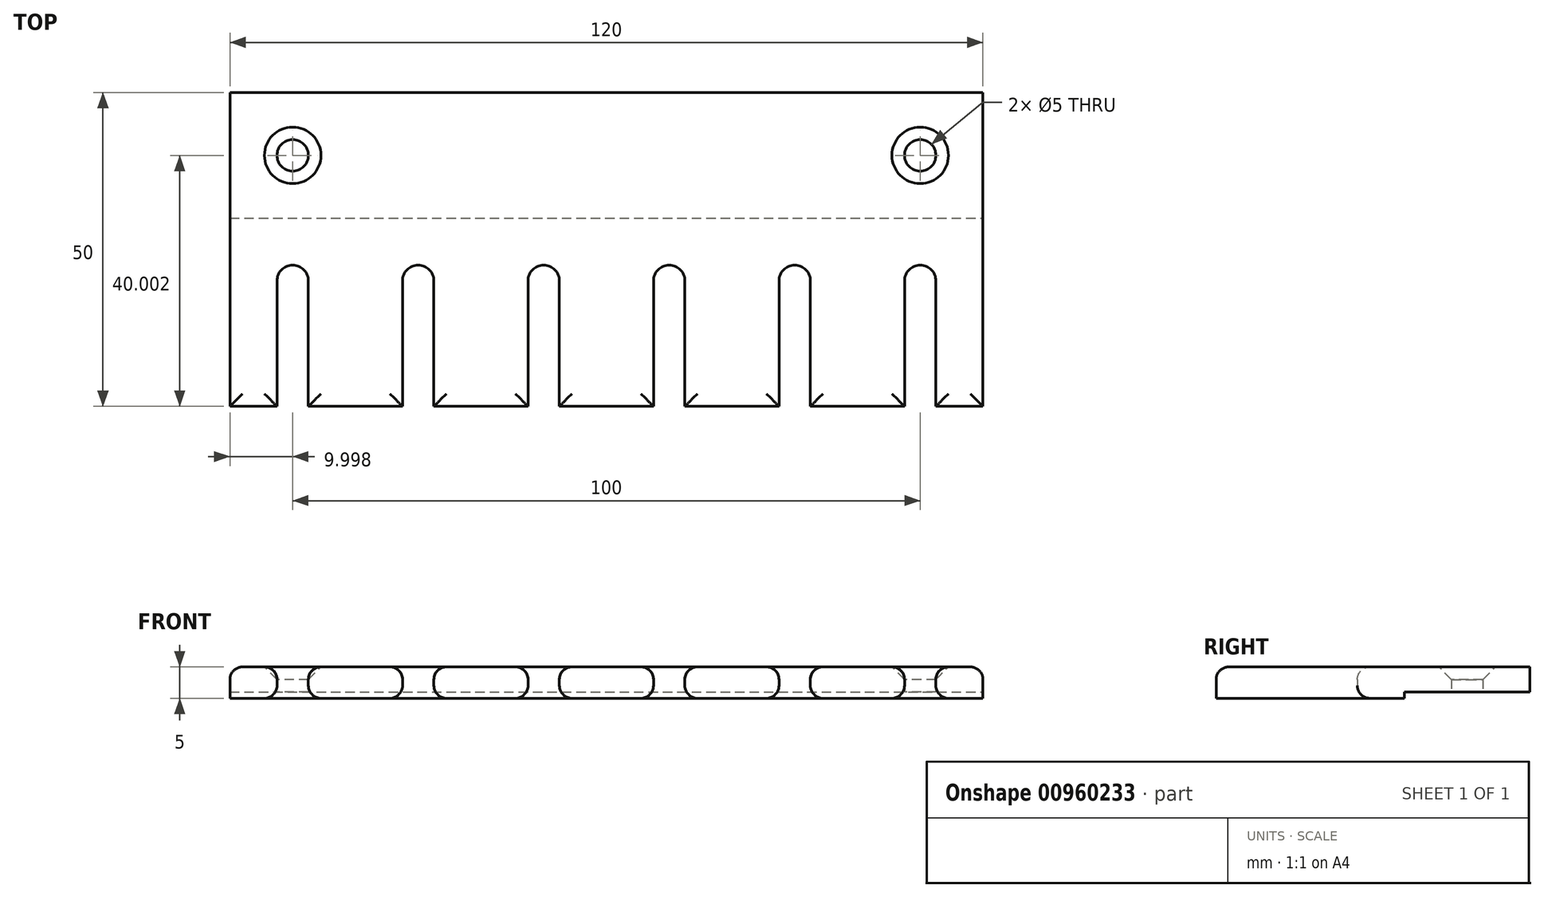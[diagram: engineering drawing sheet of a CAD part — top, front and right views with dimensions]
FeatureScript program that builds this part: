
annotation { "Feature Type Name" : "Feature", "Feature Type Description" : "" }
export const myFeature = defineFeature(function(context is Context, id is Id, definition is map)
    precondition{}
    {
        {
            var Q0;
            Q0=qCreatedBy(makeId("Top.planeOp"),FACE);
            var sketch = newSketch(context, id + "F0", { "sketchPlane" : qUnion([Q0])});
            skLineSegment(sketch, "E0.bottom", {"start": v(-45.03, 29.31) * mm, "end": v(74.97, 29.31) * mm});
            skLineSegment(sketch, "E0.top", {"start": v(-45.03, -20.69) * mm, "end": v(-37.53, -20.69) * mm});
            skLineSegment(sketch, "E0.left", {"start": v(-45.03, 29.31) * mm, "end": v(-45.03, -20.69) * mm});
            skLineSegment(sketch, "E0.right", {"start": v(74.97, 29.31) * mm, "end": v(74.97, -20.69) * mm});
            skArc(sketch, "E1", {"start": v(-32.53, -0.69) * mm, "mid": v(-35.03, 1.81) * mm, "end": v(-37.53, -0.69) * mm});
            skLineSegment(sketch, "E2", {"start": v(-32.53, -0.69) * mm, "end": v(-32.53, -20.69) * mm});
            skArc(sketch, "E3.MirrorC", {"start": v(-37.53, -0.69) * mm, "mid": v(-35.03, 1.81) * mm, "end": v(-32.53, -0.69) * mm});
            skLineSegment(sketch, "E4.MirrorCS", {"start": v(-37.53, -0.69) * mm, "end": v(-37.53, -20.69) * mm});
            skLineSegment(sketch, "E5.trimOffspring", {"start": v(-32.53, -20.69) * mm, "end": v(-17.53, -20.69) * mm});
            skLineSegment(sketch, "E6.1.0.0", {"start": v(-12.53, -0.69) * mm, "end": v(-12.53, -20.69) * mm});
            skLineSegment(sketch, "E6.1.0.1", {"start": v(-17.53, -0.69) * mm, "end": v(-17.53, -20.69) * mm});
            skArc(sketch, "E6.1.0.2", {"start": v(-12.53, -0.69) * mm, "mid": v(-15.03, 1.81) * mm, "end": v(-17.53, -0.69) * mm});
            skArc(sketch, "E6.1.0.3", {"start": v(-17.53, -0.69) * mm, "mid": v(-15.03, 1.81) * mm, "end": v(-12.53, -0.69) * mm});
            skLineSegment(sketch, "E6.2.0.0", {"start": v(7.47, -0.69) * mm, "end": v(7.47, -20.69) * mm});
            skLineSegment(sketch, "E6.2.0.1", {"start": v(2.47, -0.69) * mm, "end": v(2.47, -20.69) * mm});
            skArc(sketch, "E6.2.0.2", {"start": v(7.47, -0.69) * mm, "mid": v(4.97, 1.81) * mm, "end": v(2.47, -0.69) * mm});
            skArc(sketch, "E6.2.0.3", {"start": v(2.47, -0.69) * mm, "mid": v(4.97, 1.81) * mm, "end": v(7.47, -0.69) * mm});
            skLineSegment(sketch, "E6.3.0.0", {"start": v(27.47, -0.69) * mm, "end": v(27.47, -20.69) * mm});
            skLineSegment(sketch, "E6.3.0.1", {"start": v(22.47, -0.69) * mm, "end": v(22.47, -20.69) * mm});
            skArc(sketch, "E6.3.0.2", {"start": v(27.47, -0.69) * mm, "mid": v(24.97, 1.81) * mm, "end": v(22.47, -0.69) * mm});
            skArc(sketch, "E6.3.0.3", {"start": v(22.47, -0.69) * mm, "mid": v(24.97, 1.81) * mm, "end": v(27.47, -0.69) * mm});
            skLineSegment(sketch, "E6.4.0.0", {"start": v(47.47, -0.69) * mm, "end": v(47.47, -20.69) * mm});
            skLineSegment(sketch, "E6.4.0.1", {"start": v(42.47, -0.69) * mm, "end": v(42.47, -20.69) * mm});
            skArc(sketch, "E6.4.0.2", {"start": v(47.47, -0.69) * mm, "mid": v(44.97, 1.81) * mm, "end": v(42.47, -0.69) * mm});
            skArc(sketch, "E6.4.0.3", {"start": v(42.47, -0.69) * mm, "mid": v(44.97, 1.81) * mm, "end": v(47.47, -0.69) * mm});
            skLineSegment(sketch, "E6.5.0.0", {"start": v(67.47, -0.69) * mm, "end": v(67.47, -20.69) * mm});
            skLineSegment(sketch, "E6.5.0.1", {"start": v(62.47, -0.69) * mm, "end": v(62.47, -20.69) * mm});
            skArc(sketch, "E6.5.0.2", {"start": v(67.47, -0.69) * mm, "mid": v(64.97, 1.81) * mm, "end": v(62.47, -0.69) * mm});
            skArc(sketch, "E6.5.0.3", {"start": v(62.47, -0.69) * mm, "mid": v(64.97, 1.81) * mm, "end": v(67.47, -0.69) * mm});
            skLineSegment(sketch, "E6.direction1", {"start": v(-37.53, -20.69) * mm, "end": v(-17.53, -20.69) * mm, "construction": true});
            skCircle(sketch, "E7", {"center": v(-35.03, 19.31) * mm, "radius": 2.5 * mm});
            skCircle(sketch, "E8", {"center": v(64.97, 19.31) * mm, "radius": 2.5 * mm});
            skLineSegment(sketch, "E9.trimOffspring", {"start": v(-12.53, -20.69) * mm, "end": v(2.47, -20.69) * mm});
            skLineSegment(sketch, "E10.trimOffspring", {"start": v(7.47, -20.69) * mm, "end": v(22.47, -20.69) * mm});
            skLineSegment(sketch, "E11.trimOffspring", {"start": v(27.47, -20.69) * mm, "end": v(42.47, -20.69) * mm});
            skLineSegment(sketch, "E12.trimOffspring", {"start": v(47.47, -20.69) * mm, "end": v(62.47, -20.69) * mm});
            skLineSegment(sketch, "E13.trimOffspring", {"start": v(67.47, -20.69) * mm, "end": v(74.97, -20.69) * mm});
            skLineSegment(sketch, "E14", {"start": v(-45.03, 9.31) * mm, "end": v(74.97, 9.31) * mm});
            skPoint(sketch, "E14.endSnap0", {"position": v(74.97, 4.31) * mm});
            skSolve(sketch);
        }
        {
            var Q0;
            {var subQ4=sQuery(id+"F0.wireOp",EDGE,"E0.top");Q0=makeQuery(id+"F0.imprint","IMPRINT",FACE,{"disambiguationData":[TD([[makeQuery(id+"F0.imprint","IMPRINT",EDGE,{"derivedFrom":subQ4}),1.0]])]});}
            extrude(context, id + "F1", {"entities" : qUnion([Q0]), "depth" : 5 * mm, "offsetDistance" : 25 * mm});
        }
        {
            var Q0;
            {var subQ1=sQuery(id+"F0.wireOp",EDGE,"E0.bottom");Q0=makeQuery(id+"F0.imprint","IMPRINT",FACE,{"disambiguationData":[TD([[makeQuery(id+"F0.imprint","IMPRINT",EDGE,{"derivedFrom":subQ1}),-1.0]])]});}
            extrude(context, id + "F2", {"entities" : qUnion([Q0]), "operationType" : NewBodyOperationType.ADD, "depth" : 5 * mm, "offsetDistance" : 25 * mm, "hasSecondDirection" : true, "secondDirectionOppositeDirection" : true, "secondDirectionDepth" : -1 * mm});
        }
        {
            var Q0;
            Q0=makeQuery(id+"F2.opExtrude","CAP_EDGE",EDGE,{"disambiguationData":[OSD([sQuery(id+"F0.wireOp",EDGE,"E7")])],"isStart":false});
            var Q1;
            Q1=makeQuery(id+"F2.opExtrude","CAP_EDGE",EDGE,{"disambiguationData":[OSD([sQuery(id+"F0.wireOp",EDGE,"E8")])],"isStart":false});
            chamfer(context, id + "F3", {"entities" : qUnion([Q0, Q1]), "width" : 2 * mm, "tangentPropagation" : true});
        }
        {
            var Q0;
            Q0=makeQuery(id+"F1.opExtrude","CAP_EDGE",EDGE,{"disambiguationData":[OSD([sQuery(id+"F0.wireOp",EDGE,"E4.MirrorCS")])],"isStart":false});
            var Q1;
            Q1=makeQuery(id+"F1.opExtrude","CAP_EDGE",EDGE,{"disambiguationData":[OSD([sQuery(id+"F0.wireOp",EDGE,"E0.top")])],"isStart":false});
            var Q2;
            Q2=makeQuery(id+"F1.opExtrude","CAP_EDGE",EDGE,{"disambiguationData":[OSD([sQuery(id+"F0.wireOp",EDGE,"E5.trimOffspring")])],"isStart":false});
            var Q3;
            Q3=makeQuery(id+"F1.opExtrude","CAP_EDGE",EDGE,{"disambiguationData":[OSD([sQuery(id+"F0.wireOp",EDGE,"E6.1.0.1")])],"isStart":false});
            var Q4;
            Q4=makeQuery(id+"F1.opExtrude","CAP_EDGE",EDGE,{"disambiguationData":[OSD([sQuery(id+"F0.wireOp",EDGE,"E9.trimOffspring")])],"isStart":false});
            var Q5;
            Q5=makeQuery(id+"F1.opExtrude","CAP_EDGE",EDGE,{"disambiguationData":[OSD([sQuery(id+"F0.wireOp",EDGE,"E6.2.0.1")])],"isStart":false});
            var Q6;
            Q6=makeQuery(id+"F1.opExtrude","CAP_EDGE",EDGE,{"disambiguationData":[OSD([sQuery(id+"F0.wireOp",EDGE,"E10.trimOffspring")])],"isStart":false});
            var Q7;
            Q7=makeQuery(id+"F1.opExtrude","CAP_EDGE",EDGE,{"disambiguationData":[OSD([sQuery(id+"F0.wireOp",EDGE,"E6.3.0.1")])],"isStart":false});
            var Q8;
            Q8=makeQuery(id+"F1.opExtrude","CAP_EDGE",EDGE,{"disambiguationData":[OSD([sQuery(id+"F0.wireOp",EDGE,"E11.trimOffspring")])],"isStart":false});
            var Q9;
            Q9=makeQuery(id+"F1.opExtrude","CAP_EDGE",EDGE,{"disambiguationData":[OSD([sQuery(id+"F0.wireOp",EDGE,"E6.4.0.1")])],"isStart":false});
            var Q10;
            Q10=makeQuery(id+"F1.opExtrude","CAP_EDGE",EDGE,{"disambiguationData":[OSD([sQuery(id+"F0.wireOp",EDGE,"E12.trimOffspring")])],"isStart":false});
            var Q11;
            Q11=makeQuery(id+"F1.opExtrude","CAP_EDGE",EDGE,{"disambiguationData":[OSD([sQuery(id+"F0.wireOp",EDGE,"E6.5.0.1")])],"isStart":false});
            var Q12;
            Q12=makeQuery(id+"F1.opExtrude","CAP_EDGE",EDGE,{"disambiguationData":[OSD([sQuery(id+"F0.wireOp",EDGE,"E13.trimOffspring")])],"isStart":false});
            var Q13;
            Q13=makeQuery(id+"F1.opExtrude","CAP_EDGE",EDGE,{"disambiguationData":[OSD([sQuery(id+"F0.wireOp",EDGE,"E0.left")])],"isStart":false});
            var Q14;
            Q14=makeQuery(id+"F1.opExtrude","CAP_EDGE",EDGE,{"disambiguationData":[OSD([sQuery(id+"F0.wireOp",EDGE,"E0.right")])],"isStart":false});
            var Q15;
            Q15=makeQuery(id+"F1.opExtrude","CAP_EDGE",EDGE,{"disambiguationData":[OSD([sQuery(id+"F0.wireOp",EDGE,"E6.3.0.0")])],"isStart":true});
            var Q16;
            Q16=makeQuery(id+"F1.opExtrude","CAP_EDGE",EDGE,{"disambiguationData":[OSD([sQuery(id+"F0.wireOp",EDGE,"E6.4.0.1")])],"isStart":true});
            var Q17;
            Q17=makeQuery(id+"F1.opExtrude","CAP_EDGE",EDGE,{"disambiguationData":[OSD([sQuery(id+"F0.wireOp",EDGE,"E6.5.0.1")])],"isStart":true});
            var Q18;
            Q18=makeQuery(id+"F1.opExtrude","CAP_EDGE",EDGE,{"disambiguationData":[OSD([sQuery(id+"F0.wireOp",EDGE,"E6.2.0.1")])],"isStart":true});
            var Q19;
            Q19=makeQuery(id+"F1.opExtrude","CAP_EDGE",EDGE,{"disambiguationData":[OSD([sQuery(id+"F0.wireOp",EDGE,"E6.1.0.1")])],"isStart":true});
            var Q20;
            Q20=makeQuery(id+"F1.opExtrude","CAP_EDGE",EDGE,{"disambiguationData":[OSD([sQuery(id+"F0.wireOp",EDGE,"E2")])],"isStart":true});
            fillet(context, id + "F4", {"entities" : qUnion([Q0, Q1, Q2, Q3, Q4, Q5, Q6, Q7, Q8, Q9, Q10, Q11, Q12, Q13, Q14, Q15, Q16, Q17, Q18, Q19, Q20]), "radius" : 2 * mm, "tangentPropagation" : true, "allowEdgeOverflow" : false});
        }
    });
